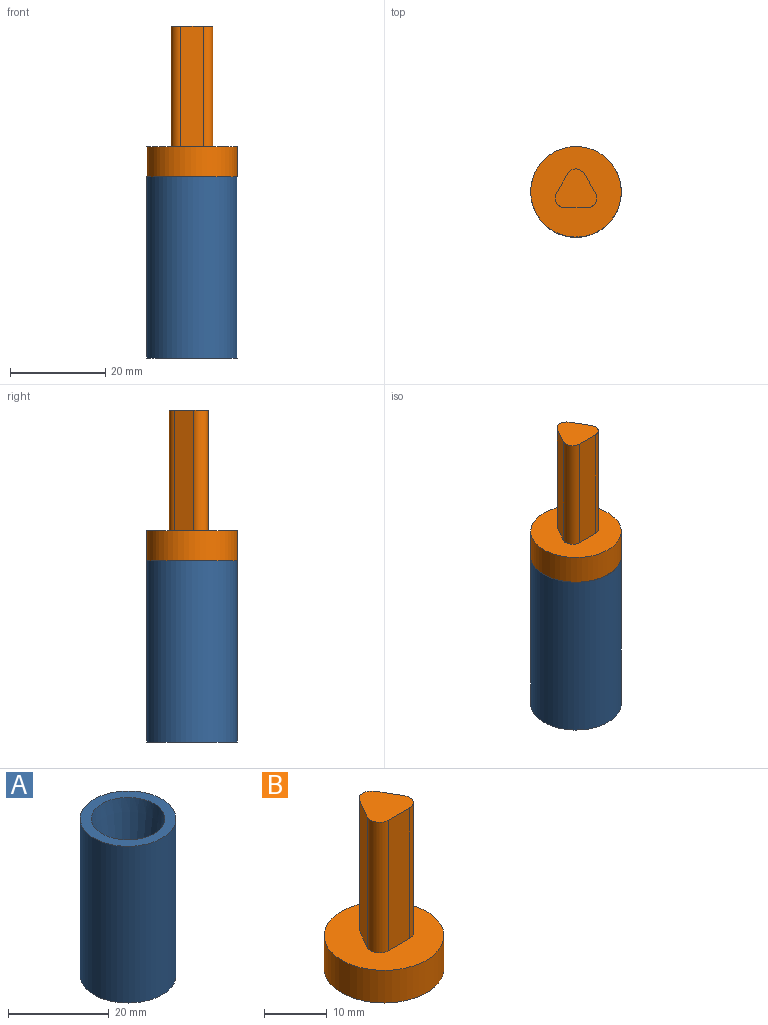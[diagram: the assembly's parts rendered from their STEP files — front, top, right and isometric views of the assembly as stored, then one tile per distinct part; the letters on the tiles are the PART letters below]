
ASSEMBLY  parts=2 mates=1
PART A: 10 faces, bbox 19.1x19.1x39.1 mm
  f0: cylinder r=9.53mm len=38.1mm, axis (0,0,-1), area 2280.2mm2, adj f1,f2
  f1: plane 19.05x19.05mm, normal (0,0,1), area 117.5mm2, adj f0,f4
  f2: plane 19.05x19.05mm, normal (0,0,-1), area 216.6mm2, adj f0,f5,f8,f9
  f3: cylinder r=4.76mm len=13.18mm, axis (0,0,1), area 382.4mm2, adj f4,f6,f7,f8,f9
  f4: cone r=4.76mm half-angle=7.6deg, axis (0,0,1), area 728.4mm2, adj f1,f3
  f5: cylinder r=3.98mm len=7.95mm, axis (0,0,1), area 1mm2, adj f2,f6,f8,f9
  f6: cone r=3.98mm half-angle=45deg, axis (0,0,1), area 9.2mm2, adj f3,f5,f8,f9
  f7: plane 0.67x0.55mm, normal (-0.95,-0.32,0), area 0.2mm2, adj f3,f8,f9
  f8: bspline ~12.33x10.68mm, area 179.6mm2, adj f2,f3,f5,f6,f7,f9
  f9: bspline ~12.33x10.68mm, area 175.2mm2, adj f2,f3,f5,f6,f7,f8
PART B: 10 faces, bbox 19.1x19.1x31.8 mm
  f0: plane 25.4x4.15mm, normal (-0.87,0.5,0), area 121.8mm2, adj f1,f5,f6,f9
  f1: cylinder r=2.03mm len=25.4mm, axis (0,0,-1), area 105.7mm2, adj f0,f2,f6,f9
  f2: plane 25.4x4.81mm, normal (0,-1,0), area 122.3mm2, adj f1,f3,f6,f9
  f3: cylinder r=2.03mm len=25.4mm, axis (0,0,-1), area 105.9mm2, adj f2,f4,f6,f9
  f4: plane 25.4x4.17mm, normal (0.87,0.5,0), area 122.3mm2, adj f3,f5,f6,f9
  f5: cylinder r=2.03mm len=25.4mm, axis (0,0,-1), area 106.5mm2, adj f0,f4,f6,f9
  f6: plane 8.79x8.16mm, normal (0,0,1), area 51.4mm2, adj f0,f1,f2,f3,f4,f5
  f7: cylinder r=9.53mm len=19.05mm, axis (0,0,1), area 380mm2, adj f8,f9
  f8: plane 19.05x19.05mm, normal (0,0,-1), area 285mm2, adj f7
  f9: plane 19.05x19.05mm, normal (0,0,1), area 233.6mm2, adj f0,f1,f2,f3,f4,f5,f7
PLACE A rot(axis=(0,1,0),180deg) t=(-23.98,-7.81,-0.98)mm
PLACE B t=(-23.98,-7.81,5.37)mm
MATE fastened A.f0 <-> B.f7  axis (0,0,1) through (-23.98,-7.81,-0.98)mm
